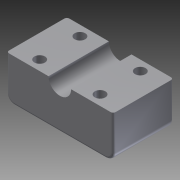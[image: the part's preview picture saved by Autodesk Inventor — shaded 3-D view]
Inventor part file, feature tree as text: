
AUTODESK INVENTOR PART (.ipt)
format: ipt  version: 2012 (Build 160160000, 160)  size: 150,528 bytes
history: native  units: mm
features: extrude x5, sketch x5, fillet x2
ambient origin geometry x8: Origin, YZ Plane, XZ Plane, XY Plane, X Axis, Y Axis, Z Axis, Center Point
bodies: Solid1 (feature_tree)
feature tree (12):
  extrude  "Extrusion1"  Depth=42.4mm
  extrude  "Extrusion2"  Depth=9.2mm
  extrude  "Extrusion3"  Depth=9.2mm
  extrude  "Extrusion4"  Depth=4.0mm
  fillet  "Fillet3"  Radius=4.0mm
  fillet  "Fillet4"  Radius=4.0mm
  extrude  "Extrusion6"  Depth=17.0mm TaperAngle=0.0deg
  sketch  "Sketch1"  dims[d0=24.0mm d1=42.4mm]
  sketch  "Sketch2"  dims[d2=4.2mm d3=9.2mm]
  sketch  "Sketch3"  dims[d4=9.2mm d5=9.2mm]
  sketch  "Sketch4"  dims[d6=9.2mm d7=4.0mm d8=4.0mm d9=4.0mm]
  sketch  "Sketch7"  dims[d10=4.0mm d11=17.0mm d12=0.0mm d13=9.0mm d14=21.2mm d15=0.0mm d16=13.5mm d17=0.0mm d20=8.5mm d21=4.0mm d22=0.0mm d23=12.3mm d24=0.0mm d25=3.0mm d26=1.0mm d35=12.0mm d36=6.0mm d37=7.5mm d38=10.0mm d39=0.0mm]
